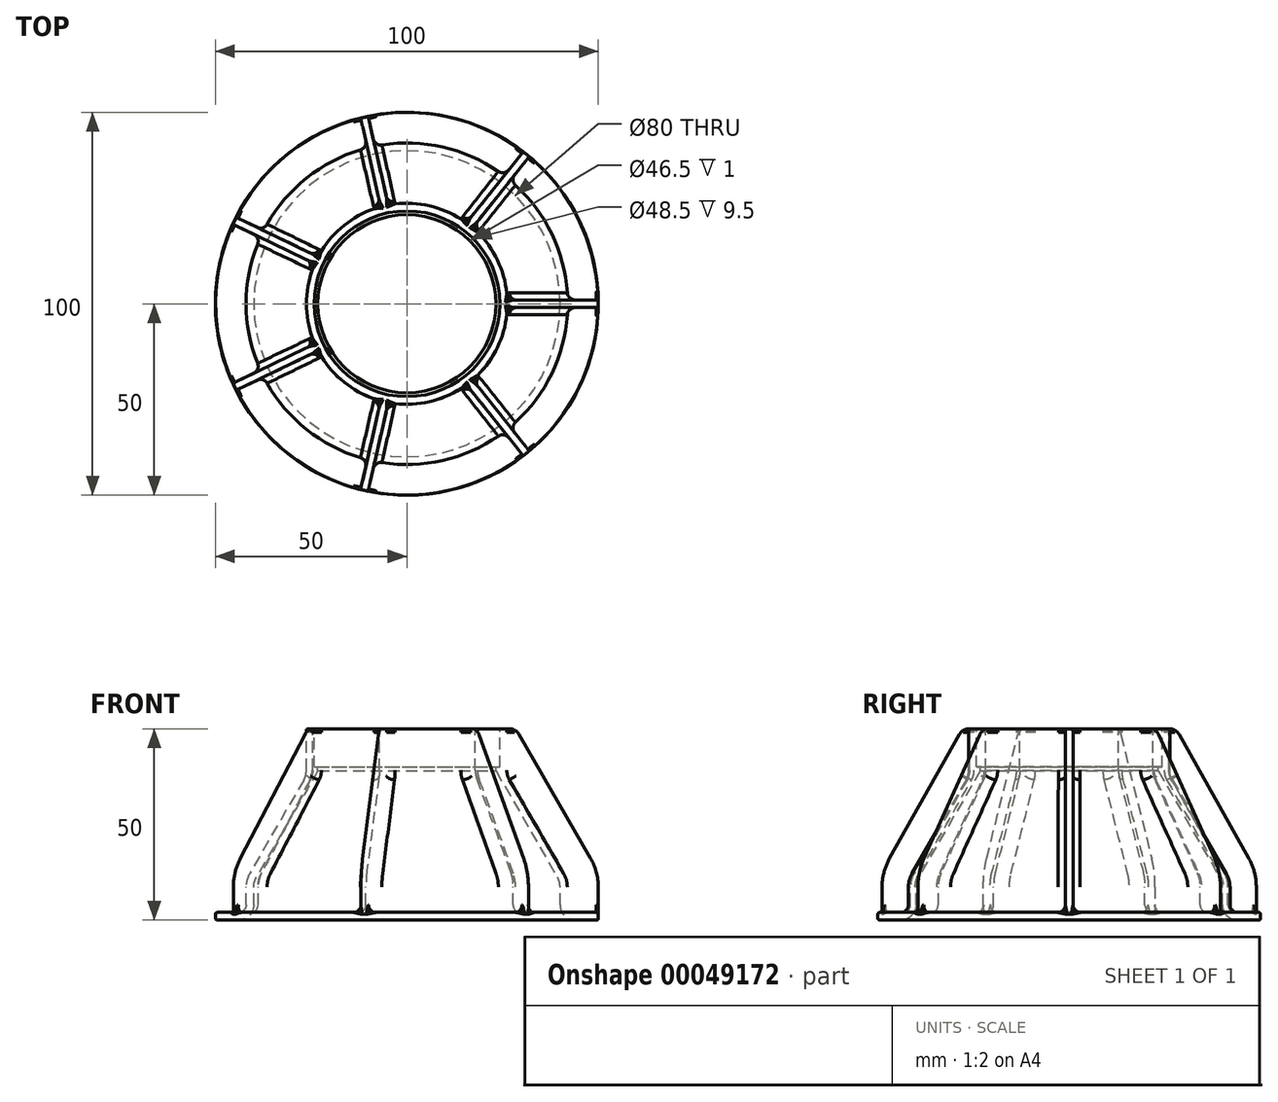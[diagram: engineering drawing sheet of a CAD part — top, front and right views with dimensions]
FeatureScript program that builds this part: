
annotation { "Feature Type Name" : "Feature", "Feature Type Description" : "" }
export const myFeature = defineFeature(function(context is Context, id is Id, definition is map)
    precondition{}
    {
        {
            var Q0;
            Q0=qCreatedBy(makeId("Front.planeOp"),FACE);
            var sketch = newSketch(context, id + "F0", { "sketchPlane" : qUnion([Q0])});
            skLineSegment(sketch, "E0", {"start": v(24.25, 0) * mm, "end": v(24.25, 10) * mm});
            skLineSegment(sketch, "E1", {"start": v(23.25, 11) * mm, "end": v(39.33, 38.85) * mm});
            skLineSegment(sketch, "E2", {"start": v(41.06, 37.85) * mm, "end": v(26.92, 13.36) * mm});
            skLineSegment(sketch, "E3", {"start": v(25.75, 0) * mm, "end": v(24.25, 0) * mm});
            skLineSegment(sketch, "E4", {"start": v(26.25, 0.5) * mm, "end": v(26.25, 10.86) * mm});
            skPoint(sketch, "E5.newPointB", {"position": v(26.56, 12.73) * mm});
            skArc(sketch, "E5.filletArc", {"start": v(26.92, 13.36) * mm, "mid": v(26.42, 12.15) * mm, "end": v(26.25, 10.86) * mm});
            skLineSegment(sketch, "E6", {"start": v(40, 41.35) * mm, "end": v(40, 46) * mm});
            skLineSegment(sketch, "E7", {"start": v(44, 50) * mm, "end": v(49.5, 50) * mm});
            skLineSegment(sketch, "E8", {"start": v(42, 46) * mm, "end": v(42, 41.35) * mm});
            skPoint(sketch, "E9.visualSharp", {"position": v(40, 40.01) * mm});
            skArc(sketch, "E9.filletArc", {"start": v(39.33, 38.85) * mm, "mid": v(39.83, 40.06) * mm, "end": v(40, 41.35) * mm});
            skArc(sketch, "E10", {"start": v(41.06, 37.85) * mm, "mid": v(41.76, 39.54) * mm, "end": v(42, 41.35) * mm});
            skLineSegment(sketch, "E11", {"start": v(44, 48) * mm, "end": v(49.5, 48) * mm});
            skLineSegment(sketch, "E12", {"start": v(50, 48.5) * mm, "end": v(50, 49.5) * mm});
            skPoint(sketch, "E13.visualSharp", {"position": v(42, 48) * mm});
            skArc(sketch, "E13.filletArc", {"start": v(44, 48) * mm, "mid": v(42.59, 47.41) * mm, "end": v(42, 46) * mm});
            skArc(sketch, "E14", {"start": v(40, 46) * mm, "mid": v(41.17, 48.83) * mm, "end": v(44, 50) * mm});
            skPoint(sketch, "E15.visualSharp", {"position": v(50, 48) * mm});
            skArc(sketch, "E15.filletArc", {"start": v(49.5, 48) * mm, "mid": v(49.85, 48.15) * mm, "end": v(50, 48.5) * mm});
            skPoint(sketch, "E16.visualSharp", {"position": v(50, 50) * mm});
            skArc(sketch, "E16.filletArc", {"start": v(50, 49.5) * mm, "mid": v(49.85, 49.85) * mm, "end": v(49.5, 50) * mm});
            skPoint(sketch, "E17.visualSharp", {"position": v(26.25, 0) * mm});
            skArc(sketch, "E17.filletArc", {"start": v(25.75, 0) * mm, "mid": v(26.1, 0.15) * mm, "end": v(26.25, 0.5) * mm});
            skLineSegment(sketch, "E18", {"start": v(0, 0) * mm, "end": v(0, 66.69) * mm});
            skLineSegment(sketch, "E19", {"start": v(24.25, 10) * mm, "end": v(23.25, 10) * mm});
            skLineSegment(sketch, "E20", {"start": v(23.25, 10) * mm, "end": v(23.25, 11) * mm});
            skPoint(sketch, "E21.orphan", {"position": v(24.25, 12.73) * mm});
            skLineSegment(sketch, "E22", {"start": v(0, 0) * mm, "end": v(-90.87, 0) * mm});
            skSolve(sketch);
        }
        {
            var Q0;
            Q0 = qSketchRegion(id + "F0", true);
            var Q1;
            Q1=sQuery(id+"F0.wireOp",EDGE,"E18");
            revolve(context, id + "F1", {"entities" : qUnion([Q0]), "axis" : qUnion([Q1]), "revolveType" : RevolveType.FULL});
        }
        {
            var Q0;
            Q0=qCreatedBy(makeId("Front.planeOp"),FACE);
            var sketch = newSketch(context, id + "F2", { "sketchPlane" : qUnion([Q0])});
            skLineSegment(sketch, "E23.0", {"start": v(24.25, 12.73) * mm, "end": v(40, 40.01) * mm});
            skLineSegment(sketch, "E24.0", {"start": v(40, 40.01) * mm, "end": v(40, 46) * mm});
            skLineSegment(sketch, "E25.0", {"start": v(24.25, 0) * mm, "end": v(24.25, 12.73) * mm});
            skLineSegment(sketch, "E26.0", {"start": v(26.71, 0) * mm, "end": v(24.25, 0) * mm});
            skPoint(sketch, "E27.orphan", {"position": v(39.33, 38.85) * mm});
            skPoint(sketch, "E28.orphan", {"position": v(40, 41.35) * mm});
            skLineSegment(sketch, "E29.0", {"start": v(50, 48.5) * mm, "end": v(41.44, 48.5) * mm});
            skLineSegment(sketch, "E30", {"start": v(29.31, 1.5) * mm, "end": v(50, 37.33) * mm});
            skLineSegment(sketch, "E31", {"start": v(50, 37.33) * mm, "end": v(50, 49.5) * mm});
            skPoint(sketch, "E32.orphan", {"position": v(25.75, 0) * mm});
            skPoint(sketch, "E33.orphan", {"position": v(-25.75, 0) * mm});
            skPoint(sketch, "E34.orphan", {"position": v(35, 0) * mm});
            skLineSegment(sketch, "E35", {"start": v(40, 46) * mm, "end": v(41.44, 48.5) * mm});
            skPoint(sketch, "E36.orphan", {"position": v(-50, 48.5) * mm});
            skPoint(sketch, "E37.0", {"position": v(35, 41.35) * mm});
            skPoint(sketch, "E38.visualSharp", {"position": v(28.45, 0) * mm});
            skArc(sketch, "E38.filletArc", {"start": v(26.71, 0) * mm, "mid": v(28.21, 0.4) * mm, "end": v(29.31, 1.5) * mm});
            skPoint(sketch, "E39.orphan", {"position": v(24.25, 10) * mm});
            skPoint(sketch, "E40.orphan", {"position": v(23.25, 11) * mm});
            skSolve(sketch);
        }
        {
            var Q0;
            Q0=makeQuery(id+"F2.imprint","IMPRINT",FACE,{"disambiguationData":[TD([[makeQuery(id+"F2.imprint","IMPRINT",EDGE,{"derivedFrom":sQuery(id+"F2.wireOp",EDGE,"E23.0")}),-1.0]])]});
            extrude(context, id + "F3", {"entities" : qUnion([Q0]), "operationType" : NewBodyOperationType.ADD, "endBound" : BoundingType.SYMMETRIC, "depth" : 2 * mm});
        }
        {
            var Q0;
            Q0=makeQuery(id+"F3.opExtrude","SWEPT_EDGE",EDGE,{"disambiguationData":[OSD([sQuery(id+"F2.wireOp",EDGE,"E30"),sQuery(id+"F2.wireOp",EDGE,"E31")])]});
            fillet(context, id + "F4", {"entities" : qUnion([Q0]), "radius" : 15 * mm, "allowEdgeOverflow" : false});
        }
        {
            var Q0;
            Q0=makeQuery(id+"F3.opExtrude","CAP_EDGE",EDGE,{"disambiguationData":[OSD([sQuery(id+"F2.wireOp",EDGE,"E31")])],"isStart":true});
            var Q1;
            Q1=makeQuery(id+"F3.opExtrude","CAP_EDGE",EDGE,{"disambiguationData":[OSD([sQuery(id+"F2.wireOp",EDGE,"E31")])],"isStart":false});
            fillet(context, id + "F5", {"entities" : qUnion([Q0, Q1]), "radius" : .5 * mm, "tangentPropagation" : true, "allowEdgeOverflow" : false});
        }
        {
            var Q0;
            Q0=makeQuery(id+"F3.boolean.opBoolean","INTERSECT",EDGE,{"derivedFrom":[makeQuery(id+"F1.opRevolve","SWEPT_FACE",FACE,{"disambiguationData":[OSD([sQuery(id+"F0.wireOp",EDGE,"E2")])]}),makeQuery(id+"F3.opExtrude","CAP_FACE",FACE,{"disambiguationData":[OSD([sQuery(id+"F2.wireOp",EDGE,"E23.0"),sQuery(id+"F2.wireOp",EDGE,"E24.0"),sQuery(id+"F2.wireOp",EDGE,"E25.0"),sQuery(id+"F2.wireOp",EDGE,"E26.0"),sQuery(id+"F2.wireOp",EDGE,"E29.0"),sQuery(id+"F2.wireOp",EDGE,"E30"),sQuery(id+"F2.wireOp",EDGE,"E31"),sQuery(id+"F2.wireOp",EDGE,"E35"),sQuery(id+"F2.wireOp",EDGE,"E38.filletArc")])],"isStart":false})]});
            var Q1;
            Q1=makeQuery(id+"F3.boolean.opBoolean","INTERSECT",EDGE,{"derivedFrom":[makeQuery(id+"F1.opRevolve","SWEPT_FACE",FACE,{"disambiguationData":[OSD([sQuery(id+"F0.wireOp",EDGE,"E2")])]}),makeQuery(id+"F3.opExtrude","CAP_FACE",FACE,{"disambiguationData":[OSD([sQuery(id+"F2.wireOp",EDGE,"E23.0"),sQuery(id+"F2.wireOp",EDGE,"E24.0"),sQuery(id+"F2.wireOp",EDGE,"E25.0"),sQuery(id+"F2.wireOp",EDGE,"E26.0"),sQuery(id+"F2.wireOp",EDGE,"E29.0"),sQuery(id+"F2.wireOp",EDGE,"E30"),sQuery(id+"F2.wireOp",EDGE,"E31"),sQuery(id+"F2.wireOp",EDGE,"E35"),sQuery(id+"F2.wireOp",EDGE,"E38.filletArc")])],"isStart":true})]});
            fillet(context, id + "F6", {"entities" : qUnion([Q0, Q1]), "radius" : 2 * mm, "tangentPropagation" : true, "allowEdgeOverflow" : false});
        }
        {
            var Q0;
            Q0=makeQuery(id+"F1.opRevolve","SWEPT_BODY",BODY,{"disambiguationData":[OSD([sQuery(id+"F0.wireOp",EDGE,"E0"),sQuery(id+"F0.wireOp",EDGE,"E1"),sQuery(id+"F0.wireOp",EDGE,"E2"),sQuery(id+"F0.wireOp",EDGE,"E3"),sQuery(id+"F0.wireOp",EDGE,"E4"),sQuery(id+"F0.wireOp",EDGE,"E5.filletArc"),sQuery(id+"F0.wireOp",EDGE,"E6"),sQuery(id+"F0.wireOp",EDGE,"E7"),sQuery(id+"F0.wireOp",EDGE,"E8"),sQuery(id+"F0.wireOp",EDGE,"E9.filletArc"),sQuery(id+"F0.wireOp",EDGE,"E10"),sQuery(id+"F0.wireOp",EDGE,"E11"),sQuery(id+"F0.wireOp",EDGE,"E12"),sQuery(id+"F0.wireOp",EDGE,"E13.filletArc"),sQuery(id+"F0.wireOp",EDGE,"E14"),sQuery(id+"F0.wireOp",EDGE,"E15.filletArc"),sQuery(id+"F0.wireOp",EDGE,"E16.filletArc"),sQuery(id+"F0.wireOp",EDGE,"E17.filletArc")])]});
            var Q1;
            Q1=sQuery(id+"F0.wireOp",EDGE,"E18");
            circularPattern(context, id + "F7", {"operationType" : NewBodyOperationType.ADD, "entities" : qUnion([Q0]), "axis" : qUnion([Q1]), "angle" : 360 * degree, "instanceCount" : 7, "equalSpace" : true});
        }
        {
            var Q0;
            Q0=makeQuery(id+"F1.opRevolve","SWEPT_BODY",BODY,{"disambiguationData":[OSD([sQuery(id+"F0.wireOp",EDGE,"E0"),sQuery(id+"F0.wireOp",EDGE,"E1"),sQuery(id+"F0.wireOp",EDGE,"E2"),sQuery(id+"F0.wireOp",EDGE,"E3"),sQuery(id+"F0.wireOp",EDGE,"E4"),sQuery(id+"F0.wireOp",EDGE,"E5.filletArc"),sQuery(id+"F0.wireOp",EDGE,"E6"),sQuery(id+"F0.wireOp",EDGE,"E7"),sQuery(id+"F0.wireOp",EDGE,"E8"),sQuery(id+"F0.wireOp",EDGE,"E9.filletArc"),sQuery(id+"F0.wireOp",EDGE,"E10"),sQuery(id+"F0.wireOp",EDGE,"E11"),sQuery(id+"F0.wireOp",EDGE,"E12"),sQuery(id+"F0.wireOp",EDGE,"E13.filletArc"),sQuery(id+"F0.wireOp",EDGE,"E14"),sQuery(id+"F0.wireOp",EDGE,"E15.filletArc"),sQuery(id+"F0.wireOp",EDGE,"E16.filletArc"),sQuery(id+"F0.wireOp",EDGE,"E17.filletArc"),sQuery(id+"F0.wireOp",EDGE,"E19"),sQuery(id+"F0.wireOp",EDGE,"E20")])]});
            var Q1;
            Q1=sQuery(id+"F0.wireOp",EDGE,"E22");
            transform(context, id + "F8", {"entities" : qUnion([Q0]), "transformType" : TransformType.ROTATION, "transformAxis" : qUnion([Q1]), "angle" : 180 * degree, "makeCopy" : false});
        }
        {
            var Q0;
            Q0=makeQuery(id+"F1.opRevolve","SWEPT_EDGE",EDGE,{"disambiguationData":[OSD([sQuery(id+"F0.wireOp",EDGE,"E0"),sQuery(id+"F0.wireOp",EDGE,"E3")])]});
            fillet(context, id + "F9", {"entities" : qUnion([Q0]), "radius" : 0.5 * mm, "tangentPropagation" : true, "allowEdgeOverflow" : false});
        }
    });
